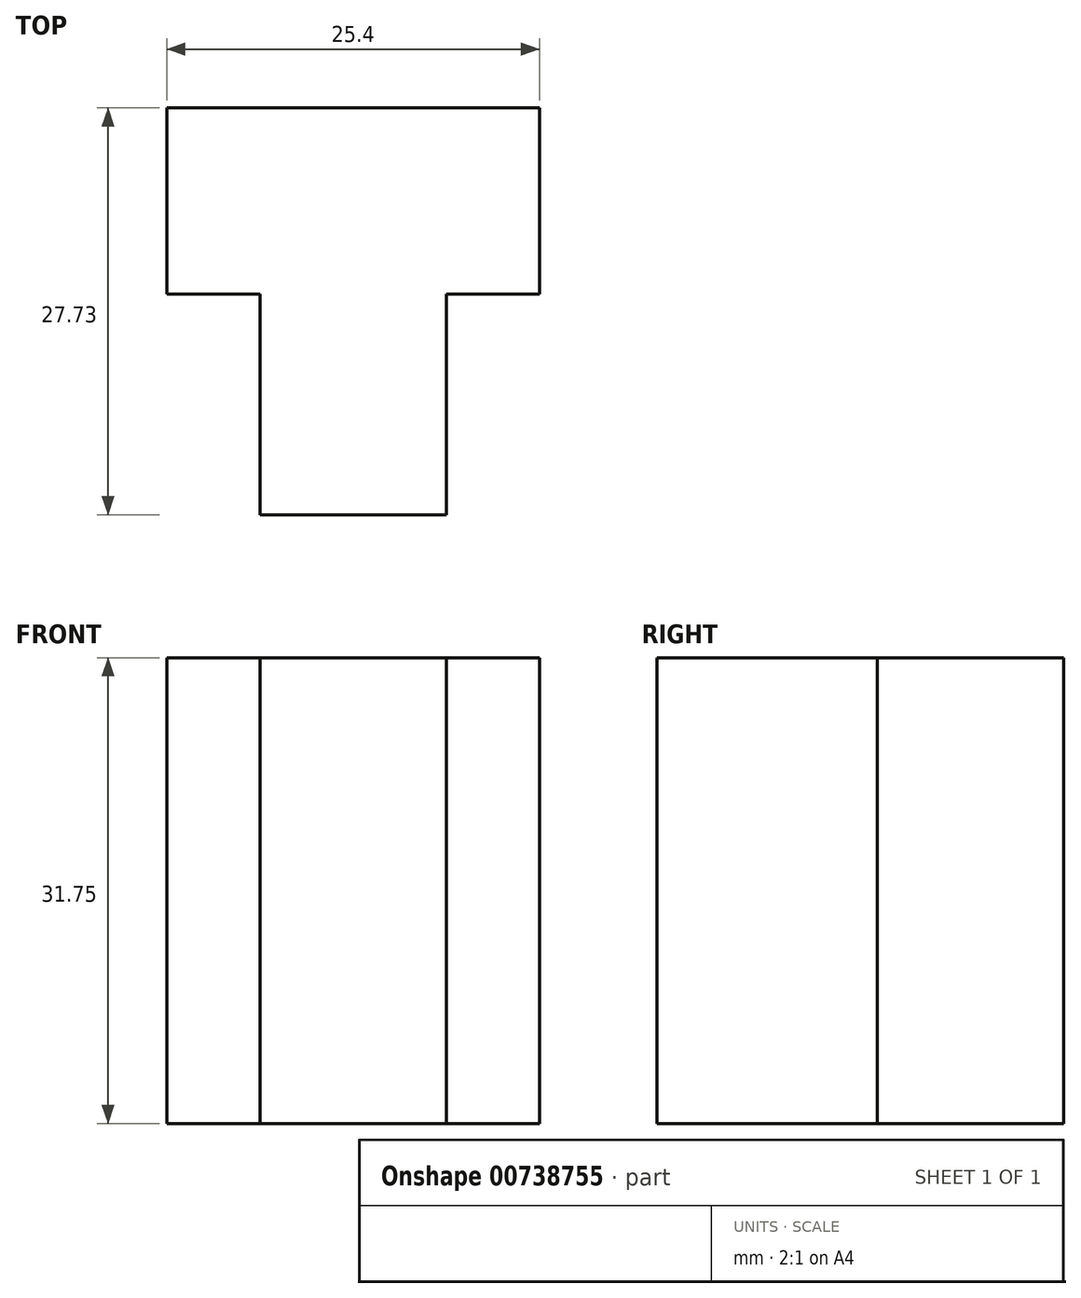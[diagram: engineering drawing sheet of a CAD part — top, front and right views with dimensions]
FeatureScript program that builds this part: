
annotation { "Feature Type Name" : "Feature", "Feature Type Description" : "" }
export const myFeature = defineFeature(function(context is Context, id is Id, definition is map)
    precondition{}
    {
        {
            var Q0;
            Q0=qCreatedBy(makeId("Top.planeOp"),FACE);
            var sketch = newSketch(context, id + "F0", { "sketchPlane" : qUnion([Q0])});
            skLineSegment(sketch, "E0", {"start": v(0, 0) * mm, "end": v(-12.7, 0) * mm});
            skLineSegment(sketch, "E1", {"start": v(-12.7, 0) * mm, "end": v(-12.7, 15.03) * mm});
            skLineSegment(sketch, "E2", {"start": v(-12.7, 15.03) * mm, "end": v(-19.05, 15.03) * mm});
            skLineSegment(sketch, "E3", {"start": v(-19.05, 15.03) * mm, "end": v(-19.05, 27.73) * mm});
            skLineSegment(sketch, "E4", {"start": v(-19.05, 27.73) * mm, "end": v(6.35, 27.73) * mm});
            skLineSegment(sketch, "E5", {"start": v(6.35, 27.73) * mm, "end": v(6.35, 15.03) * mm});
            skLineSegment(sketch, "E6", {"start": v(6.35, 15.03) * mm, "end": v(0, 15.03) * mm});
            skLineSegment(sketch, "E7", {"start": v(0, 15.03) * mm, "end": v(0, 0) * mm});
            skSolve(sketch);
        }
        {
            var Q0;
            Q0 = qSketchRegion(id + "F0", true);
            extrude(context, id + "F1", {"entities" : qUnion([Q0]), "depth" : 31.75 * mm, "offsetDistance" : 25.4 * mm});
        }
    });
